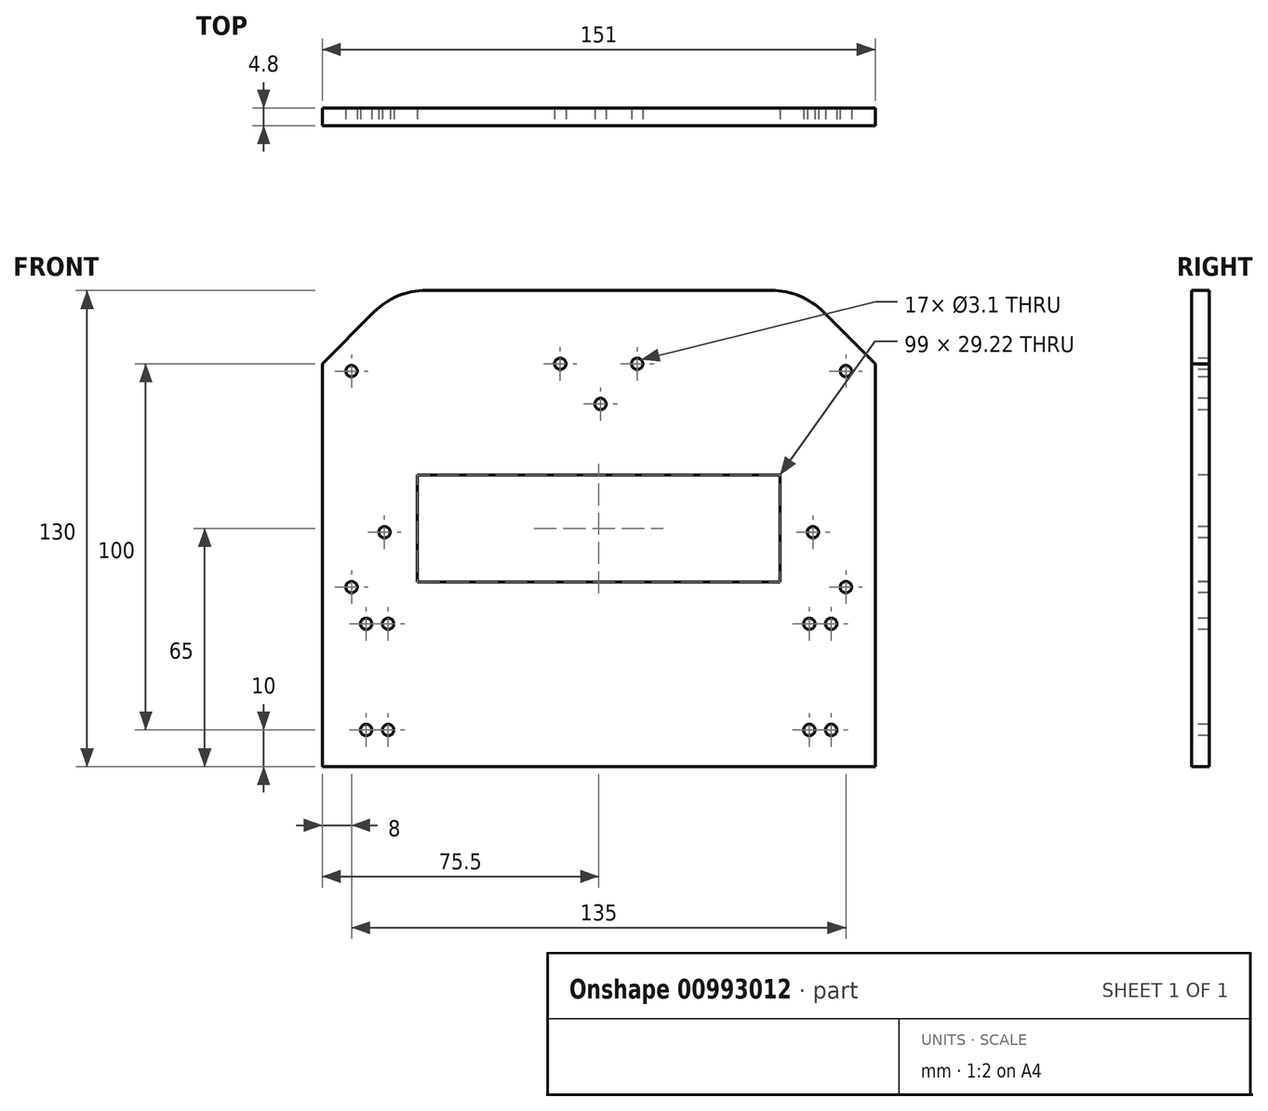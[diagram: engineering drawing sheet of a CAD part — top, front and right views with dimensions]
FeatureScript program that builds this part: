
annotation { "Feature Type Name" : "Feature", "Feature Type Description" : "" }
export const myFeature = defineFeature(function(context is Context, id is Id, definition is map)
    precondition{}
    {
        {
            var Q0;
            Q0=qCreatedBy(makeId("Front.planeOp"),FACE);
            var sketch = newSketch(context, id + "F0", { "sketchPlane" : qUnion([Q0])});
            skLineSegment(sketch, "E0.bottom", {"start": v(75.5, -65) * mm, "end": v(-75.5, -65) * mm});
            skLineSegment(sketch, "E0.top", {"start": v(75.5, 65) * mm, "end": v(-75.5, 65) * mm});
            skLineSegment(sketch, "E0.left", {"start": v(75.5, -65) * mm, "end": v(75.5, 65) * mm});
            skLineSegment(sketch, "E0.right", {"start": v(-75.5, -65) * mm, "end": v(-75.5, 65) * mm});
            skPoint(sketch, "E0.middle", {"position": v(0, 0) * mm});
            skSolve(sketch);
        }
        {
            var Q0;
            Q0=makeQuery(id+"F0.imprint","IMPRINT",FACE,{"disambiguationData":[TD([[makeQuery(id+"F0.imprint","IMPRINT",EDGE,{"derivedFrom":sQuery(id+"F0.wireOp",EDGE,"E0.bottom")}),-1.0]])]});
            extrude(context, id + "F1", {"entities" : qUnion([Q0]), "depth" : 4.8 * mm, "offsetDistance" : 25 * mm});
        }
        {
            var Q0;
            Q0=makeQuery(id+"F1.opExtrude","CAP_FACE",FACE,{"disambiguationData":[OSD([sQuery(id+"F0.wireOp",EDGE,"E0.bottom"),sQuery(id+"F0.wireOp",EDGE,"E0.top"),sQuery(id+"F0.wireOp",EDGE,"E0.left"),sQuery(id+"F0.wireOp",EDGE,"E0.right")])],"isStart":false});
            var sketch = newSketch(context, id + "F2", { "sketchPlane" : qUnion([Q0])});
            skLineSegment(sketch, "E1.bottom", {"start": v(49.5, 14.61) * mm, "end": v(-49.5, 14.61) * mm});
            skLineSegment(sketch, "E1.top", {"start": v(49.5, -14.61) * mm, "end": v(-49.5, -14.61) * mm});
            skLineSegment(sketch, "E1.left", {"start": v(49.5, 14.61) * mm, "end": v(49.5, -14.61) * mm});
            skLineSegment(sketch, "E1.right", {"start": v(-49.5, 14.61) * mm, "end": v(-49.5, -14.61) * mm});
            skPoint(sketch, "E1.middle", {"position": v(0, 0) * mm});
            skCircle(sketch, "E2", {"center": v(-63.5, -55) * mm, "radius": 1.55 * mm});
            skCircle(sketch, "E3", {"center": v(-57.5, -55) * mm, "radius": 1.55 * mm});
            skCircle(sketch, "E4", {"center": v(-63.5, -26) * mm, "radius": 1.55 * mm});
            skCircle(sketch, "E5", {"center": v(-57.5, -26) * mm, "radius": 1.55 * mm});
            skCircle(sketch, "E6", {"center": v(57.5, -26) * mm, "radius": 1.55 * mm});
            skCircle(sketch, "E7", {"center": v(63.5, -26) * mm, "radius": 1.55 * mm});
            skCircle(sketch, "E8", {"center": v(57.5, -55) * mm, "radius": 1.55 * mm});
            skCircle(sketch, "E9", {"center": v(63.5, -55) * mm, "radius": 1.55 * mm});
            skCircle(sketch, "E10", {"center": v(-67.5, -16) * mm, "radius": 1.55 * mm});
            skCircle(sketch, "E11", {"center": v(67.5, -16) * mm, "radius": 1.55 * mm});
            skCircle(sketch, "E12", {"center": v(-58.5, -1) * mm, "radius": 1.55 * mm});
            skCircle(sketch, "E13", {"center": v(58.5, -1) * mm, "radius": 1.55 * mm});
            skCircle(sketch, "E14", {"center": v(67.5, 43) * mm, "radius": 1.55 * mm});
            skCircle(sketch, "E15", {"center": v(-67.5, 43) * mm, "radius": 1.55 * mm});
            skCircle(sketch, "E16", {"center": v(-10.5, 45) * mm, "radius": 1.55 * mm});
            skCircle(sketch, "E17", {"center": v(10.5, 45) * mm, "radius": 1.55 * mm});
            skCircle(sketch, "E18", {"center": v(0.5, 34) * mm, "radius": 1.55 * mm});
            skSolve(sketch);
        }
        {
            var Q0;
            Q0=makeQuery(id+"F2.imprint","IMPRINT",FACE,{"disambiguationData":[TD([[makeQuery(id+"F2.imprint","IMPRINT",EDGE,{"derivedFrom":sQuery(id+"F2.wireOp",EDGE,"E1.bottom")}),1.0]])]});
            extrude(context, id + "F3", {"entities" : qUnion([Q0]), "operationType" : NewBodyOperationType.REMOVE, "oppositeDirection" : true, "depth" : 4.8 * mm, "offsetDistance" : 25 * mm});
        }
        {
            var Q0;
            Q0 = qSketchRegion(id + "F2", true);
            extrude(context, id + "F4", {"entities" : qUnion([Q0]), "operationType" : NewBodyOperationType.REMOVE, "oppositeDirection" : true, "depth" : 4.8 * mm, "offsetDistance" : 25 * mm});
        }
        {
            var Q0;
            Q0=makeQuery(id+"F1.opExtrude","SWEPT_EDGE",EDGE,{"disambiguationData":[OSD([sQuery(id+"F0.wireOp",EDGE,"E0.top"),sQuery(id+"F0.wireOp",EDGE,"E0.right")])]});
            chamfer(context, id + "F5", {"entities" : qUnion([Q0]), "width" : 20 * mm, "tangentPropagation" : true});
        }
        {
            var Q0;
            Q0=makeQuery(id+"F1.opExtrude","SWEPT_EDGE",EDGE,{"disambiguationData":[OSD([sQuery(id+"F0.wireOp",EDGE,"E0.top"),sQuery(id+"F0.wireOp",EDGE,"E0.left")])]});
            chamfer(context, id + "F6", {"entities" : qUnion([Q0]), "width" : 20 * mm, "tangentPropagation" : true});
        }
        {
            var Q0;
            {var subQ0=sQuery(id+"F0.wireOp",EDGE,"E0.top");Q0=makeQuery(id+"F5.opChamfer","BLEND_EDGE",EDGE,{"blendedFrom":[makeQuery(id+"F1.opExtrude","SWEPT_EDGE",EDGE,{"disambiguationData":[OSD([subQ0,sQuery(id+"F0.wireOp",EDGE,"E0.right")])]}),makeQuery(id+"F1.opExtrude","SWEPT_FACE",FACE,{"disambiguationData":[OSD([subQ0])]})],"blendedInto":[makeQuery(id+"F1.opExtrude","SWEPT_FACE",FACE,{"disambiguationData":[OSD([subQ0])]})]});}
            fillet(context, id + "F7", {"entities" : qUnion([Q0]), "radius" : 20 * mm, "tangentPropagation" : true, "allowEdgeOverflow" : false});
        }
        {
            var Q0;
            {var subQ0=sQuery(id+"F0.wireOp",EDGE,"E0.top");Q0=makeQuery(id+"F6.opChamfer","BLEND_EDGE",EDGE,{"blendedFrom":[makeQuery(id+"F1.opExtrude","SWEPT_EDGE",EDGE,{"disambiguationData":[OSD([subQ0,sQuery(id+"F0.wireOp",EDGE,"E0.left")])]}),makeQuery(id+"F1.opExtrude","SWEPT_FACE",FACE,{"disambiguationData":[OSD([subQ0])]})],"blendedInto":[makeQuery(id+"F1.opExtrude","SWEPT_FACE",FACE,{"disambiguationData":[OSD([subQ0])]})]});}
            fillet(context, id + "F8", {"entities" : qUnion([Q0]), "radius" : 20 * mm, "tangentPropagation" : true, "allowEdgeOverflow" : false});
        }
    });
